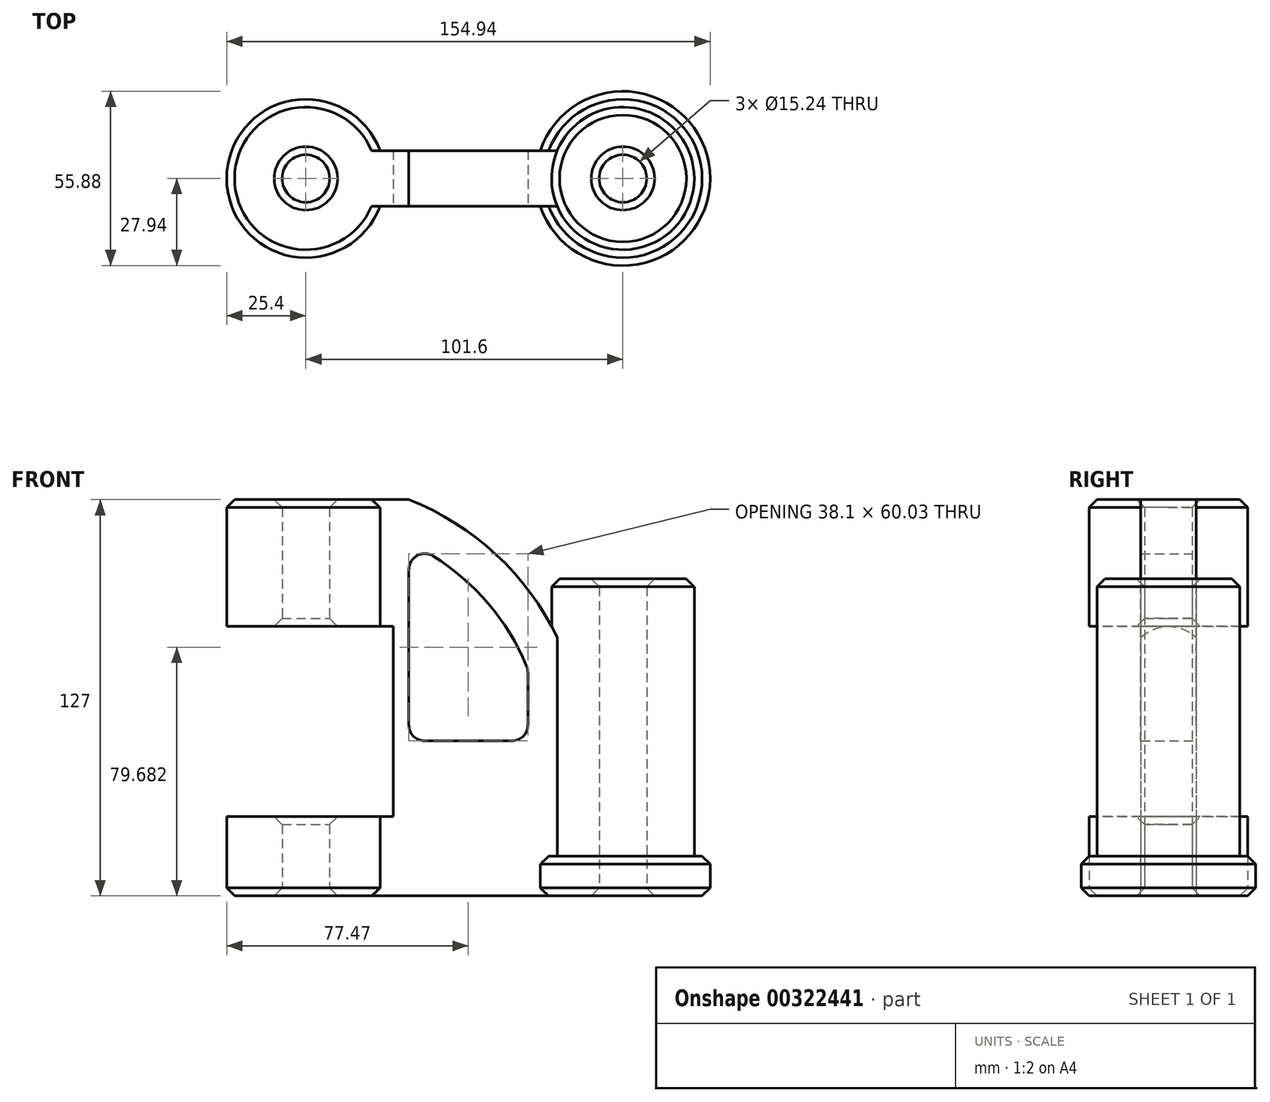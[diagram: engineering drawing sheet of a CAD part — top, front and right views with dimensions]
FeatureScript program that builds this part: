
annotation { "Feature Type Name" : "Feature", "Feature Type Description" : "" }
export const myFeature = defineFeature(function(context is Context, id is Id, definition is map)
    precondition{}
    {
        {
            var Q0;
            Q0=qCreatedBy(makeId("Top.planeOp"),FACE);
            var sketch = newSketch(context, id + "F0", { "sketchPlane" : qUnion([Q0])});
            skCircle(sketch, "E0", {"center": v(0, 0) * mm, "radius": 25.4 * mm});
            skCircle(sketch, "E1", {"center": v(0, 0) * mm, "radius": 7.62 * mm});
            skCircle(sketch, "E2", {"center": v(101.6, 0) * mm, "radius": 22.86 * mm});
            skCircle(sketch, "E3", {"center": v(101.6, 0) * mm, "radius": 7.62 * mm});
            skSolve(sketch);
        }
        {
            var Q0;
            Q0=makeQuery(id+"F0.imprint","IMPRINT",FACE,{"disambiguationData":[TD([[makeQuery(id+"F0.imprint","IMPRINT",EDGE,{"derivedFrom":sQuery(id+"F0.wireOp",EDGE,"E0")}),1.0]])]});
            extrude(context, id + "F1", {"entities" : qUnion([Q0]), "depth" : 127 * mm});
        }
        {
            var Q0;
            Q0=makeQuery(id+"F0.imprint","IMPRINT",FACE,{"disambiguationData":[TD([[makeQuery(id+"F0.imprint","IMPRINT",EDGE,{"derivedFrom":sQuery(id+"F0.wireOp",EDGE,"E2")}),1.0]])]});
            extrude(context, id + "F2", {"entities" : qUnion([Q0]), "depth" : 101.6 * mm});
        }
        {
            var Q0;
            Q0=qCreatedBy(makeId("Front.planeOp"),FACE);
            var sketch = newSketch(context, id + "F3", { "sketchPlane" : qUnion([Q0])});
            skLineSegment(sketch, "E4", {"start": v(20.32, 0) * mm, "end": v(20.32, 127) * mm});
            skLineSegment(sketch, "E5", {"start": v(20.32, 127) * mm, "end": v(33.02, 127) * mm});
            skArc(sketch, "E6", {"start": v(81.28, 81.28) * mm, "mid": v(61.58, 108.82) * mm, "end": v(33.02, 127) * mm});
            skLineSegment(sketch, "E7", {"start": v(81.28, 81.28) * mm, "end": v(81.28, 0) * mm});
            skLineSegment(sketch, "E8", {"start": v(81.28, 0) * mm, "end": v(20.32, 0) * mm});
            skArc(sketch, "E9.0", {"start": v(71.12, 72.77) * mm, "mid": v(55.88, 96.56) * mm, "end": v(33.02, 113.17) * mm});
            skLineSegment(sketch, "E10", {"start": v(33.02, 113.17) * mm, "end": v(33.02, 49.67) * mm});
            skLineSegment(sketch, "E11", {"start": v(33.02, 49.67) * mm, "end": v(71.12, 49.67) * mm});
            skLineSegment(sketch, "E12", {"start": v(71.12, 49.67) * mm, "end": v(71.12, 72.77) * mm});
            skSolve(sketch);
        }
        {
            var Q0;
            Q0=makeQuery(id+"F3.imprint","IMPRINT",FACE,{"disambiguationData":[TD([[makeQuery(id+"F3.imprint","IMPRINT",EDGE,{"derivedFrom":sQuery(id+"F3.wireOp",EDGE,"E4")}),-1.0]])]});
            extrude(context, id + "F4", {"entities" : qUnion([Q0]), "operationType" : NewBodyOperationType.ADD, "depth" : 17.78 * mm, "symmetric" : true});
        }
        {
            var Q0;
            Q0=qCreatedBy(makeId("Front.planeOp"),FACE);
            var sketch = newSketch(context, id + "F5", { "sketchPlane" : qUnion([Q0])});
            skLineSegment(sketch, "E13.bottom", {"start": v(-33.02, 86.36) * mm, "end": v(27.94, 86.36) * mm});
            skLineSegment(sketch, "E13.top", {"start": v(-33.02, 25.4) * mm, "end": v(27.94, 25.4) * mm});
            skLineSegment(sketch, "E13.left", {"start": v(-33.02, 86.36) * mm, "end": v(-33.02, 25.4) * mm});
            skLineSegment(sketch, "E13.right", {"start": v(27.94, 86.36) * mm, "end": v(27.94, 25.4) * mm});
            skSolve(sketch);
        }
        {
            var Q0;
            Q0 = qSketchRegion(id + "F5", true);
            extrude(context, id + "F6", {"entities" : qUnion([Q0]), "operationType" : NewBodyOperationType.REMOVE, "oppositeDirection" : true, "depth" : 101.6 * mm, "symmetric" : true});
        }
        {
            var Q0;
            Q0=makeQuery(id+"F4.opExtrude","SWEPT_EDGE",EDGE,{"disambiguationData":[OSD([sQuery(id+"F3.wireOp",EDGE,"E10"),sQuery(id+"F3.wireOp",EDGE,"E11")])]});
            var Q1;
            Q1=makeQuery(id+"F4.opExtrude","SWEPT_EDGE",EDGE,{"disambiguationData":[OSD([sQuery(id+"F3.wireOp",EDGE,"E11"),sQuery(id+"F3.wireOp",EDGE,"E12")])]});
            var Q2;
            Q2=makeQuery(id+"F4.opExtrude","SWEPT_EDGE",EDGE,{"disambiguationData":[OSD([sQuery(id+"F3.wireOp",EDGE,"E9.0"),sQuery(id+"F3.wireOp",EDGE,"E12")])]});
            var Q3;
            Q3=makeQuery(id+"F4.opExtrude","SWEPT_EDGE",EDGE,{"disambiguationData":[OSD([sQuery(id+"F3.wireOp",EDGE,"E9.0"),sQuery(id+"F3.wireOp",EDGE,"E10")])]});
            fillet(context, id + "F7", {"entities" : qUnion([Q0, Q1, Q2, Q3]), "radius" : 5.08 * mm, "tangentPropagation" : true, "allowEdgeOverflow" : false});
        }
        {
            var Q0;
            Q0=makeQuery(id+"F1.opExtrude","CAP_EDGE",EDGE,{"disambiguationData":[OSD([sQuery(id+"F0.wireOp",EDGE,"E0")])],"isStart":false});
            var Q1;
            Q1=makeQuery(id+"F1.opExtrude","CAP_EDGE",EDGE,{"disambiguationData":[OSD([sQuery(id+"F0.wireOp",EDGE,"E1")])],"isStart":false});
            var Q2;
            Q2=makeQuery(id+"F6.boolean.opBoolean","INTERSECT",EDGE,{"derivedFrom":[makeQuery(id+"F1.opExtrude","SWEPT_FACE",FACE,{"disambiguationData":[OSD([sQuery(id+"F0.wireOp",EDGE,"E1")])]}),makeQuery(id+"F6.opExtrude","SWEPT_FACE",FACE,{"disambiguationData":[OSD([sQuery(id+"F5.wireOp",EDGE,"E13.top")])]})]});
            var Q3;
            Q3=makeQuery(id+"F6.boolean.opBoolean","INTERSECT",EDGE,{"derivedFrom":[makeQuery(id+"F1.opExtrude","SWEPT_FACE",FACE,{"disambiguationData":[OSD([sQuery(id+"F0.wireOp",EDGE,"E1")])]}),makeQuery(id+"F6.opExtrude","SWEPT_FACE",FACE,{"disambiguationData":[OSD([sQuery(id+"F5.wireOp",EDGE,"E13.bottom")])]})]});
            var Q4;
            Q4=makeQuery(id+"F1.opExtrude","CAP_EDGE",EDGE,{"disambiguationData":[OSD([sQuery(id+"F0.wireOp",EDGE,"E0")])],"isStart":true});
            var Q5;
            Q5=makeQuery(id+"F1.opExtrude","CAP_EDGE",EDGE,{"disambiguationData":[OSD([sQuery(id+"F0.wireOp",EDGE,"E1")])],"isStart":true});
            chamfer(context, id + "F8", {"entities" : qUnion([Q0, Q1, Q2, Q3, Q4, Q5]), "width" : 2.54 * mm, "tangentPropagation" : true});
        }
        {
            var Q0;
            Q0=qCreatedBy(makeId("Top.planeOp"),FACE);
            var sketch = newSketch(context, id + "F9", { "sketchPlane" : qUnion([Q0])});
            skCircle(sketch, "E14.0", {"center": v(101.6, 0) * mm, "radius": 22.86 * mm});
            skCircle(sketch, "E15.0", {"center": v(101.6, 0) * mm, "radius": 27.94 * mm});
            skSolve(sketch);
        }
        {
            var Q0;
            Q0 = qSketchRegion(id + "F9", true);
            extrude(context, id + "F10", {"entities" : qUnion([Q0]), "operationType" : NewBodyOperationType.ADD, "depth" : 12.7 * mm});
        }
        {
            var Q0;
            Q0=makeQuery(id+"F2.opExtrude","CAP_EDGE",EDGE,{"disambiguationData":[OSD([sQuery(id+"F0.wireOp",EDGE,"E3")])],"isStart":false});
            var Q1;
            Q1=makeQuery(id+"F2.opExtrude","CAP_EDGE",EDGE,{"disambiguationData":[OSD([sQuery(id+"F0.wireOp",EDGE,"E2")])],"isStart":false});
            var Q2;
            Q2=makeQuery(id+"F10.opExtrude","CAP_EDGE",EDGE,{"disambiguationData":[OSD([sQuery(id+"F9.wireOp",EDGE,"E15.0")])],"isStart":false});
            var Q3;
            Q3=makeQuery(id+"F10.opExtrude","CAP_EDGE",EDGE,{"disambiguationData":[OSD([sQuery(id+"F9.wireOp",EDGE,"E15.0")])],"isStart":true});
            var Q4;
            Q4=makeQuery(id+"F2.opExtrude","CAP_EDGE",EDGE,{"disambiguationData":[OSD([sQuery(id+"F0.wireOp",EDGE,"E3")])],"isStart":true});
            chamfer(context, id + "F11", {"entities" : qUnion([Q0, Q1, Q2, Q3, Q4]), "width" : 2.54 * mm, "tangentPropagation" : true});
        }
    });
